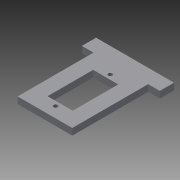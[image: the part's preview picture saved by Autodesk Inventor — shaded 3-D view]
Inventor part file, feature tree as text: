
AUTODESK INVENTOR PART (.ipt)
format: ipt  version: 2013 (Build 170138000, 138)  size: 100,864 bytes
history: native  units: mm
features: other x3, extrude x1, sketch x1
ambient origin geometry x8: Origin, YZ Plane, XZ Plane, XY Plane, X Axis, Y Axis, Z Axis, Center Point
bodies: Solid1 (feature_tree)
feature tree (5):
  other  "Blocks"
  extrude  "Extrusion1"  Depth=3.0mm
  sketch  "Sketch1"  dims[d0=3.0mm d2=3.0mm d3=0.1mm d4=38.5mm d6=7.0mm d7=22.5mm d8=12.4mm d9=4.5mm d10=4.5mm d11=2.0mm d12=2.0mm d15=3.0mm d17=27.0mm d19=3.0mm d20=37.5mm d21=3.25mm d22=0.0mm]
  other  "Block1"
  other  "Block1:1"
